# Revit family: ledfalcon-p_96w-ble2-840_523003011100
name_source: partatom
category: Lighting Fixtures
units: mm (PartAtom-declared; Revit-internal decimal feet)

## family parameters
Cut with Voids When Loaded = No
Host = Face
Light Source = No
Part Type = Normal
Room Calculation Point = No
Round Connector Dimension = Use Diameter
Shared = No

## types (1)
- LEDFalcon-P 96W-BLE2-840 (1 x LED, 12500 lm, 4000)
    Apparent Load = 96 VA
    Approval mark = CE, ENEC
    CIE Flux Codes = 48 81 97 28 100
    Color Rendering = 80
    Color Temperature = 4000
    Control Gear = Electronic ballast
    Default Elevation = 1800 mm
    Description = Modern free-floor standing luminaire with direct/indirect light distribution. Extremely comfortable light (UGR<16). Stylish touch button control on pole. Integrated motion and daylight sensor. High efficacy of 125 lm/W. App control via Smart App, possible
    Frequency = 60 Hz
    Height = 2055 mm
    Lamp = 1 x LED
    Lamp Light Flux = 12500 lm
    Lamp count = 1
    Length = 751 mm
    Luminous efficacy = 130 lm/W
    Manufacturer = OPPLE
    ModVariant = No
    Model = 523003011100
    Mounting Place = Floor
    Mounting Type = Freestanding
    Number of Poles = 1
    OnlyDefault = Yes
    Power Factor = 1
    Product Name = LEDFalcon-P 96W-BLE2-840
    Product group = Freestanding uplighter
    ProductGroupID = 13
    Protection Class = Protection class I
    Protection Degree = IP 20
    RLX_Detail_Level = 1
    RlxData = <blob elided: 94337 chars, md5=c7e001c9>
    Socket = socket
    Standby Power = 0 W
    System Light Flux = 12512 lm
    System Power = 96 W
    Type Comments = Product without accessories
    Type Image = web_falcon.jpg
    URL = http://relux.com
    VarID = ---
    Voltage = 230 V
    Voltage Range = 220-240 V
    Weight = 0.00 kg
    Width = 395 mm

## geometry (parser evidence)
native form markers: Blend x4, Sweep x15
no freeform markers — native parametric forms only
